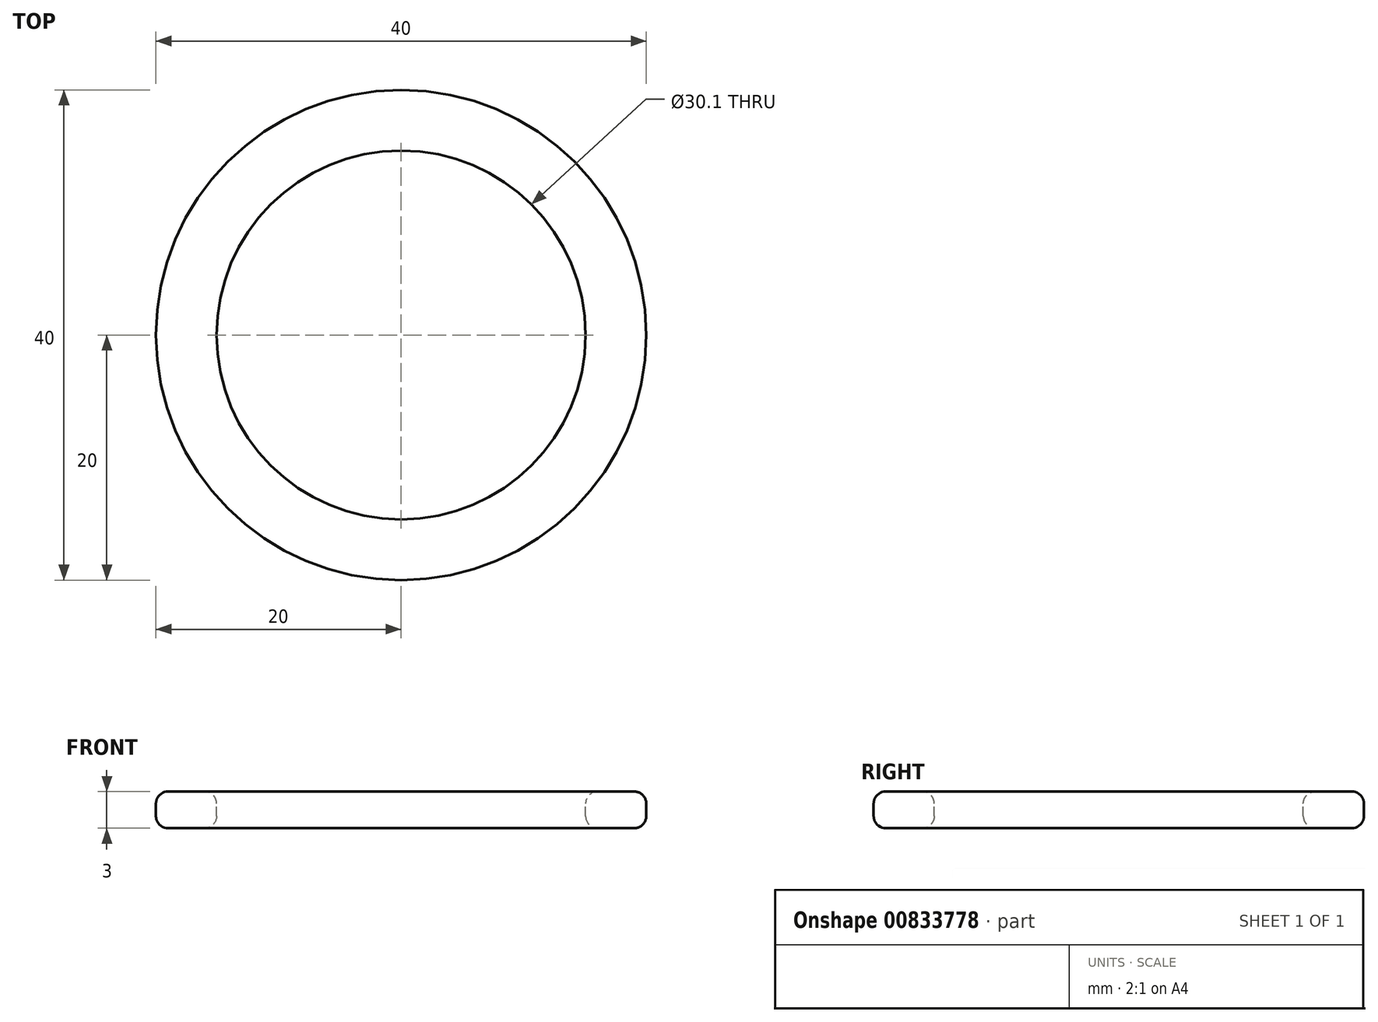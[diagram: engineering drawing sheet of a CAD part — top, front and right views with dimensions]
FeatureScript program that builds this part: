
annotation { "Feature Type Name" : "Feature", "Feature Type Description" : "" }
export const myFeature = defineFeature(function(context is Context, id is Id, definition is map)
    precondition{}
    {
        {
            var Q0;
            Q0=qCreatedBy(makeId("Front.planeOp"),FACE);
            var sketch = newSketch(context, id + "F0", { "sketchPlane" : qUnion([Q0])});
            skLineSegment(sketch, "E0.bottom", {"start": v(15.05, 0) * mm, "end": v(20, 0) * mm});
            skLineSegment(sketch, "E0.top", {"start": v(15.05, 3) * mm, "end": v(20, 3) * mm});
            skLineSegment(sketch, "E0.left", {"start": v(15.05, 0) * mm, "end": v(15.05, 3) * mm});
            skLineSegment(sketch, "E0.right", {"start": v(20, 0) * mm, "end": v(20, 3) * mm});
            skLineSegment(sketch, "E1", {"start": v(0, 17.06) * mm, "end": v(0, -11.94) * mm, "construction": true});
            skSolve(sketch);
        }
        {
            var Q0;
            Q0 = qSketchRegion(id + "F0", true);
            var Q1;
            Q1=sQuery(id+"F0.wireOp",EDGE,"E1");
            revolve(context, id + "F1", {"surfaceOperationType" : NewSurfaceOperationType.NEW, "entities" : qUnion([Q0]), "axis" : qUnion([Q1]), "revolveType" : RevolveType.FULL});
        }
        {
            var Q0;
            Q0=makeQuery(id+"F1.opRevolve","SWEPT_FACE",FACE,{"disambiguationData":[OSD([sQuery(id+"F0.wireOp",EDGE,"E0.bottom")])]});
            var Q1;
            Q1=makeQuery(id+"F1.opRevolve","SWEPT_FACE",FACE,{"disambiguationData":[OSD([sQuery(id+"F0.wireOp",EDGE,"E0.top")])]});
            fillet(context, id + "F2", {"entities" : qUnion([Q0, Q1]), "tangentPropagation" : true, "radius" : 1 * mm, "defaultsChanged" : false, "vertexSettings" : [], "allowEdgeOverflow" : false});
        }
    });
